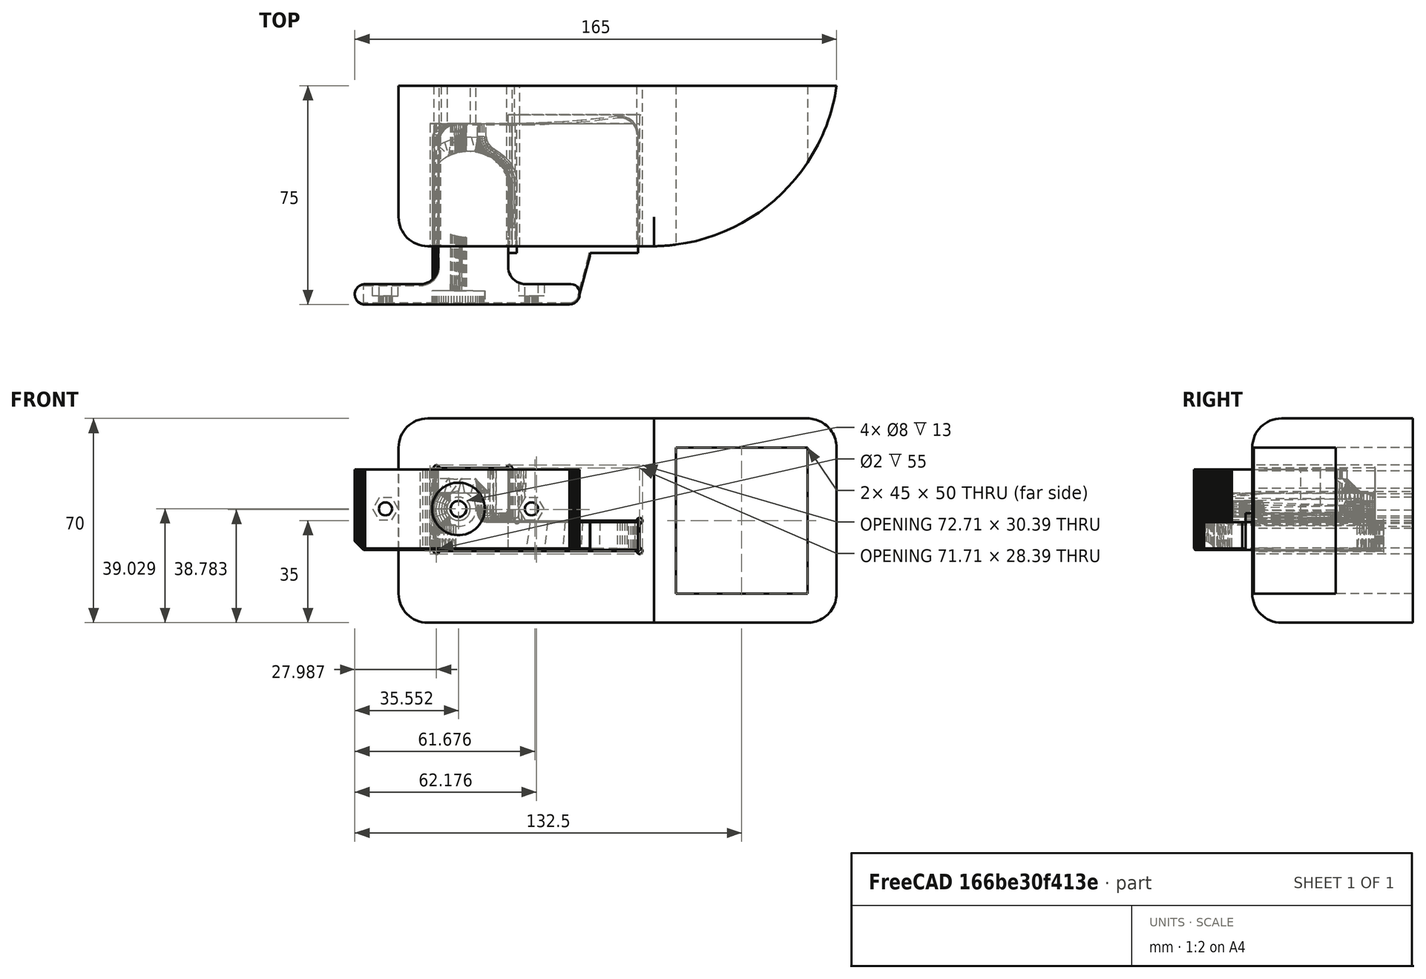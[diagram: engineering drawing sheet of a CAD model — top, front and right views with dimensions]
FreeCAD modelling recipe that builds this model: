
FCSTD DOCUMENT  (FreeCAD 0.17R7458 (Git))
Label: flexystruder_body_holderV0.7
License: CreativeCommons Attribution-ShareAlike
LicenseURL: http://creativecommons.org/licenses/by-sa/4.0/
objects: Sketcher::SketchObject×16, PartDesign::Pocket×9, PartDesign::Body×9, Part::Feature×8, PartDesign::Fillet×7, PartDesign::Pad×6, Mesh::Feature×1, PartDesign::Chamfer×1, Part::Cut×1, App::Part×1
note: 72 computed .brp shape members not serialized (recipe doc carries the construction recipe); baked Part::Feature solids carry a one-line shape summary decoded from their .brp

FEATURE [Mesh::Feature] flexystruder_body_hex_v2_0  label="flexystruder_body_hex_v2.0"
FEATURE [Part::Feature] flexystruder_body_hex_v2_0001
  shape: bbox 97.06 x 64.55 x 27.5 mm, 7934 faces, 0 solids (baked)
FEATURE [Part::Feature] flexystruder_body_hex_v2_0001001  label="flexystruder_body_hex_v2_0002"
  shape: bbox 97.06 x 64.55 x 27.5 mm, 4378 faces, 0 solids (baked)
FEATURE [Part::Feature] flexystruder_body_hex_v2_0001001_solid  label="flexystruder_body_hex_v2_0002 (Solid)"
  shape: bbox 97.06 x 64.55 x 27.5 mm, 4378 faces (baked)
FEATURE [Sketcher::SketchObject] Sketch
  MapMode = 5
  Placement = pos=(0,0,0) rot=(1,0,0;3.14159rad)
  Support = -> [flexystruder_body_hex_v2_0001001_solid]
  sketch-geometry (17):
    g0: ArcOfCircle CenterX=28 CenterY=-45.596 CenterZ=0 NormalX=0 NormalY=0 NormalZ=1 Radius=4.20615 StartAngle=4.71239 EndAngle=7.85398
    g1: ArcOfCircle CenterX=25 CenterY=-45.596 CenterZ=0 NormalX=0 NormalY=0 NormalZ=1 Radius=4.20615 StartAngle=1.5708 EndAngle=4.71239
    g2: LineSegment StartX=28 StartY=-41.3899 StartZ=0 EndX=25 EndY=-41.3899 EndZ=0
    g3: LineSegment StartX=28 StartY=-49.8022 StartZ=0 EndX=25 EndY=-49.8022 EndZ=0
    g4: ArcOfCircle CenterX=52.7327 CenterY=-58.2604 CenterZ=0 NormalX=0 NormalY=0 NormalZ=1 Radius=4.37439 StartAngle=1.5708 EndAngle=4.71239
    g5: ArcOfCircle CenterX=55.547 CenterY=-58.2604 CenterZ=0 NormalX=0 NormalY=0 NormalZ=1 Radius=4.37439 StartAngle=4.71239 EndAngle=7.85398
    g6: LineSegment StartX=52.7327 StartY=-62.6347 StartZ=0 EndX=55.547 EndY=-62.6347 EndZ=0
    g7: LineSegment StartX=52.7327 StartY=-53.886 StartZ=0 EndX=55.547 EndY=-53.886 EndZ=0
    g8: ArcOfCircle CenterX=41 CenterY=-17.6915 CenterZ=0 NormalX=0 NormalY=0 NormalZ=1 Radius=4.05397 StartAngle=4.71239 EndAngle=7.85398
    g9: ArcOfCircle CenterX=37.752 CenterY=-17.6915 CenterZ=0 NormalX=0 NormalY=0 NormalZ=1 Radius=4.05397 StartAngle=1.5708 EndAngle=4.71239
    g10: LineSegment StartX=41 StartY=-13.6375 StartZ=0 EndX=37.752 EndY=-13.6375 EndZ=0
    g11: LineSegment StartX=41 StartY=-21.7455 StartZ=0 EndX=37.752 EndY=-21.7455 EndZ=0
    g12: LineSegment StartX=23.6875 StartY=-6 StartZ=0 EndX=35.6731 EndY=-6 EndZ=0
    g13: LineSegment StartX=16.4026 StartY=-28 StartZ=0 EndX=28.3058 EndY=-28 EndZ=0
    g14: LineSegment StartX=28.3058 StartY=-28 StartZ=0 EndX=35.6731 EndY=-6 EndZ=0
    g15: LineSegment StartX=16.4026 StartY=-28 StartZ=0 EndX=16.4026 EndY=-12.5849 EndZ=0
    g16: ArcOfCircle CenterX=23.5917 CenterY=-13.2161 CenterZ=0 NormalX=0 NormalY=0 NormalZ=1 Radius=7.21677 StartAngle=1.55753 EndAngle=3.05401
  constraints (26):
    c: Tangent(g0,g3) = 1.5708
    c: Tangent(g0,g2) = -1.5708
    c: Tangent(g2,g1) = -1.5708
    c: Tangent(g3,g1) = 1.5708
    c: Horizontal(g2)
    c: Equal(g0,g1)
    c: Tangent(g4,g7) = 1.5708
    c: Tangent(g4,g6) = -1.5708
    c: Tangent(g6,g5) = -1.5708
    c: Tangent(g7,g5) = 1.5708
    c: Horizontal(g6)
    c: Equal(g4,g5)
    c: Tangent(g8,g11) = 1.5708
    c: Tangent(g8,g10) = -1.5708
    c: Tangent(g10,g9) = -1.5708
    c: Tangent(g11,g9) = 1.5708
    c: Horizontal(g10)
    c: Equal(g8,g9)
    c: Horizontal(g12)
    c: Horizontal(g13)
    c: Coincident(g14,g13)
    c: Coincident(g14,g12)
    c: Coincident(g15,g13)
    c: Vertical(g15)
    c: Coincident(g16,g12)
    c: Coincident(g16,g15)
FEATURE [PartDesign::Pad] Pad
  BaseFeature = -> flexystruder_body_hex_v2_0001001_solid
  Length = 9.5
  Length2 = 100
  Profile = -> Sketch
  Reversed = true
  Type = 0
FEATURE [Sketcher::SketchObject] Sketch001
  ExternalGeometry = -> [Pad]
  MapMode = 5
  Placement = pos=(17.5,0,0) rot=(0.57735,0.57735,0.57735;2.0944rad)
  Support = -> [Pad]
  sketch-geometry (4):
    g0: LineSegment StartX=26.5 StartY=12.5 StartZ=0 EndX=17.6702 EndY=12.5 EndZ=0
    g1: LineSegment StartX=17.6702 StartY=12.5 StartZ=0 EndX=17.6702 EndY=9.5 EndZ=0
    g2: LineSegment StartX=17.6702 StartY=9.5 StartZ=0 EndX=26.5 EndY=9.5 EndZ=0
    g3: LineSegment StartX=26.5 StartY=9.5 StartZ=0 EndX=26.5 EndY=12.5 EndZ=0
  constraints (10):
    c: Coincident(g0,g1)
    c: Coincident(g1,g2)
    c: Coincident(g2,g3)
    c: Coincident(g3,g0)
    c: Horizontal(g0)
    c: Horizontal(g2)
    c: Vertical(g1)
    c: Vertical(g3)
    c: Coincident(g0,g-4)
    c: PointOnObject(g1,g-3)
FEATURE [PartDesign::Pad] Pad001
  BaseFeature = -> Pad
  Length = 3
  Length2 = 100
  Profile = -> Sketch001
  Type = 0
FEATURE [PartDesign::Chamfer] Chamfer
  Base = -> Pad001 [Edge1475]
  BaseFeature = -> Pad001
  Size = 2.9
FEATURE [Sketcher::SketchObject] Sketch002
  ExternalGeometry = -> [Chamfer]
  MapMode = 5
  Placement = pos=(0,0,27.5) rot=(0,0,1;0rad)
  Support = -> [Chamfer]
  sketch-geometry (4):
    g0: LineSegment StartX=-6.5 StartY=48.2121 StartZ=0 EndX=-6.5 EndY=27.0119 EndZ=0
    g1: ArcOfCircle CenterX=3.84323 CenterY=38.0759 CenterZ=0 NormalX=0 NormalY=0 NormalZ=1 Radius=14.4819 StartAngle=0.364009 EndAngle=2.3663
    g2: LineSegment StartX=17.3762 StartY=43.2318 StartZ=0 EndX=17.5 EndY=37.4236 EndZ=0
    g3: ArcOfCircle CenterX=3.40646 CenterY=37.0436 CenterZ=0 NormalX=0 NormalY=0 NormalZ=1 Radius=14.0987 StartAngle=3.93327 EndAngle=6.31015
  constraints (10):
    c: Vertical(g0)
    c: Coincident(g0,g-5)
    c: Coincident(g0,g-6)
    c: Coincident(g1,g0)
    c: Coincident(g1,g-9)
    c: PointOnObject(g-21,g1)
    c: Coincident(g2,g1)
    c: Coincident(g2,g-7)
    c: Coincident(g3,g0)
    c: Coincident(g3,g2)
FEATURE [PartDesign::Pad] Pad002
  BaseFeature = -> Chamfer
  Length = 10
  Length2 = 100
  Profile = -> Sketch002
  Reversed = true
  Type = 3
  UpToFace = -> Chamfer [Face709]
FEATURE [Sketcher::SketchObject] Sketch003
  ExternalGeometry = -> [Pad002]
  MapMode = 5
  Placement = pos=(0,0,0) rot=(1,0,0;3.14159rad)
  Support = -> [Pad002]
  sketch-geometry (4):
    g0: LineSegment StartX=62.0584 StartY=-58.2729 StartZ=0 EndX=17.5 EndY=-58.2729 EndZ=0
    g1: LineSegment StartX=17.5 StartY=-58.2729 StartZ=0 EndX=17.5 EndY=-17.6702 EndZ=0
    g2: LineSegment StartX=17.5 StartY=-17.6702 StartZ=0 EndX=62.0584 EndY=-17.6702 EndZ=0
    g3: LineSegment StartX=62.0584 StartY=-17.6702 StartZ=0 EndX=62.0584 EndY=-58.2729 EndZ=0
  constraints (10):
    c: Coincident(g0,g1)
    c: Coincident(g1,g2)
    c: Coincident(g2,g3)
    c: Coincident(g3,g0)
    c: Horizontal(g0)
    c: Horizontal(g2)
    c: Vertical(g1)
    c: Vertical(g3)
    c: Coincident(g0,g-3)
    c: Coincident(g1,g-4)
FEATURE [PartDesign::Pad] Pad003
  BaseFeature = -> Pad002
  Length = 9.5
  Length2 = 100
  Profile = -> Sketch003
  Reversed = true
  Type = 0
FEATURE [Sketcher::SketchObject] Sketch005
  MapMode = 5
  Placement = pos=(0,0,0) rot=(0.57735,0.57735,0.57735;2.0944rad)
  Support = -> [YZ_Plane003]
  sketch-geometry (4):
    g0: LineSegment StartX=20 StartY=45 StartZ=0 EndX=75 EndY=45 EndZ=0
    g1: LineSegment StartX=75 StartY=45 StartZ=0 EndX=75 EndY=-25 EndZ=0
    g2: LineSegment StartX=75 StartY=-25 StartZ=0 EndX=20 EndY=-25 EndZ=0
    g3: LineSegment StartX=20 StartY=-25 StartZ=0 EndX=20 EndY=45 EndZ=0
  constraints (12):
    c: Coincident(g0,g1)
    c: Coincident(g1,g2)
    c: Coincident(g2,g3)
    c: Coincident(g3,g0)
    c: Horizontal(g0)
    c: Horizontal(g2)
    c: Vertical(g1)
    c: Vertical(g3)
    c: DistanceY(g1) = -70
    c: DistanceY(g-1,g2) = -25
    c: DistanceX(g-1,g1) = 75
    c: DistanceX(g2) = -55
FEATURE [PartDesign::Pad] Pad004002
  Length = 130
  Length2 = 20
  Placement = pos=(0,0,0) rot=(0.57735,0.57735,0.57735;2.0944rad)
  Profile = -> Sketch005
  Type = 4
FEATURE [Sketcher::SketchObject] Sketch011
  MapMode = 5
  Placement = pos=(0,62,0) rot=(1,0,0;1.5708rad)
  sketch-geometry (1):
    g0: Circle CenterX=0.546326 CenterY=14.034 CenterZ=0 NormalX=0 NormalY=0 NormalZ=1 Radius=4.18499
FEATURE [Part::Feature] Pocket003001  label="Pocket004"
  shape: bbox 155.2 x 62.65 x 70 mm, 98 faces (baked)
FEATURE [Sketcher::SketchObject] Sketch004
  ExternalGeometry = -> [Pad003]
  MapMode = 5
  Placement = pos=(0,20,0) rot=(1,0,0;1.5708rad)
  Support = -> [Pocket003001]
  constraints (10):
    c: Coincident(g0,g1)
    c: Coincident(g1,g2)
    c: Coincident(g2,g3)
    c: Coincident(g3,g0)
    c: Horizontal(g0)
    c: Horizontal(g2)
    c: Vertical(g1)
    c: Vertical(g3)
    c: Coincident(g0,g-4)
    c: Coincident(g1,g-3)
FEATURE [PartDesign::Pad] Pad004
  BaseFeature = -> Pocket003001
  Length = 1
  Length2 = 100
  Profile = -> Sketch004
  Reversed = true
  Type = 0
FEATURE [Sketcher::SketchObject] Sketch012
  MapMode = 5
  Placement = pos=(0,20,0) rot=(1,0,0;1.5708rad)
  Support = -> [Pocket003001]
  sketch-geometry (3):
    g0: LineSegment StartX=17.5433 StartY=12.8629 StartZ=0 EndX=21.0794 EndY=9.39905 EndZ=0
    g1: LineSegment StartX=21.0794 StartY=9.39905 StartZ=0 EndX=17.4196 EndY=9.04442 EndZ=0
    g2: LineSegment StartX=17.4196 StartY=9.04442 StartZ=0 EndX=17.5433 EndY=12.8629 EndZ=0
  constraints (3):
    c: Coincident(g0,g1)
    c: Coincident(g1,g2)
    c: Coincident(g2,g0)
FEATURE [PartDesign::Pocket] Pocket003002
  BaseFeature = -> Pocket003001
  Length = 5
  Profile = -> Sketch012
  Type = 2
FEATURE [Part::Feature] Pocket003002001  label="Pocket003003"
  shape: bbox 155.2 x 62.65 x 70 mm, 96 faces (baked)
FEATURE [Sketcher::SketchObject] Sketch013
  ExternalGeometry = -> [Pocket003002001]
  MapMode = 5
  Placement = pos=(0,62,0) rot=(1,0,0;1.5708rad)
  Support = -> [Pocket003002001]
  sketch-geometry (4):
    g0: LineSegment StartX=62.5298 StartY=-0.412097 StartZ=0 EndX=17.5 EndY=-0.412097 EndZ=0
    g1: LineSegment StartX=17.5 StartY=-0.412097 StartZ=0 EndX=17.5 EndY=9.93195 EndZ=0
    g2: LineSegment StartX=17.5 StartY=9.93195 StartZ=0 EndX=62.5298 EndY=9.93195 EndZ=0
    g3: LineSegment StartX=62.5298 StartY=9.93195 StartZ=0 EndX=62.5298 EndY=-0.412097 EndZ=0
  constraints (11):
    c: Coincident(g0,g1)
    c: Coincident(g1,g2)
    c: Coincident(g2,g3)
    c: Coincident(g3,g0)
    c: Horizontal(g0)
    c: Horizontal(g2)
    c: Vertical(g1)
    c: Vertical(g3)
    c: Coincident(g0,g-5)
    c: PointOnObject(g-3,g2)
    c: PointOnObject(g-4,g1)
FEATURE [PartDesign::Pocket] Pocket003002002
  BaseFeature = -> Pocket003002001
  Length = 3
  Profile = -> Sketch013
  Type = 0
FEATURE [Sketcher::SketchObject] Sketch014
  ExternalGeometry = -> [Pocket003002002]
  MapMode = 5
  Placement = pos=(0,20,0) rot=(1,0,0;1.5708rad)
  Support = -> [Pocket003002002]
  sketch-geometry (9):
    g0: Circle CenterX=17.9124 CenterY=12.5014 CenterZ=0 NormalX=0 NormalY=0 NormalZ=1 Radius=1
    g1: Circle CenterX=20.5354 CenterY=9.93195 CenterZ=0 NormalX=0 NormalY=0 NormalZ=1 Radius=1
    g2: Circle CenterX=62.5298 CenterY=9.93195 CenterZ=0 NormalX=0 NormalY=0 NormalZ=1 Radius=1
    g3: Circle CenterX=62.5298 CenterY=-0.412097 CenterZ=0 NormalX=0 NormalY=0 NormalZ=1 Radius=1
    g4: Circle CenterX=-7.01255 CenterY=-0.412097 CenterZ=0 NormalX=0 NormalY=0 NormalZ=1 Radius=1
    g5: Circle CenterX=-7.01255 CenterY=8.30665 CenterZ=0 NormalX=0 NormalY=0 NormalZ=1 Radius=1
    g6: Circle CenterX=-7.01858 CenterY=20.0686 CenterZ=0 NormalX=0 NormalY=0 NormalZ=1 Radius=1
    g7: Circle CenterX=-7.01858 CenterY=27.9783 CenterZ=0 NormalX=0 NormalY=0 NormalZ=1 Radius=1
    g8: Circle CenterX=17.9124 CenterY=27.9783 CenterZ=0 NormalX=0 NormalY=0 NormalZ=1 Radius=1
  constraints (18):
    c: Coincident(g0,g-4)
    c: Coincident(g1,g-5)
    c: Coincident(g2,g-6)
    c: Coincident(g3,g-7)
    c: Coincident(g4,g-7)
    c: Coincident(g5,g-8)
    c: Coincident(g6,g-8)
    c: Coincident(g7,g-3)
    c: Coincident(g8,g-4)
    c: Radius(g7) = 1
    c: Equal(g7,g6)
    c: Equal(g7,g5)
    c: Equal(g7,g4)
    c: Equal(g7,g1)
    c: Equal(g7,g0)
    c: Equal(g7,g8)
    c: Equal(g7,g2)
    c: Equal(g7,g3)
FEATURE [PartDesign::Pocket] Pocket003002003
  BaseFeature = -> Pocket003002002
  Length = 0
  Profile = -> Sketch014
  Type = 1
FEATURE [Part::Feature] Pocket003002003001  label="Pocket003002004"
  shape: bbox 155.2 x 62.65 x 70 mm, 57 faces (baked)
FEATURE [PartDesign::Fillet] Fillet001
  Base = -> Pocket003002003001 [Edge94,Edge89,Edge98,Edge96]
  BaseFeature = -> Pocket003002003001
  Radius = 1
FEATURE [Part::Feature] Fillet001001  label="Fillet002"
  shape: bbox 155.2 x 62.65 x 70 mm, 61 faces (baked)
FEATURE [PartDesign::Fillet] Fillet001002
  Base = -> Fillet001001 [Edge115,Edge114]
  BaseFeature = -> Fillet001001
  Radius = 1
FEATURE [PartDesign::Fillet] Fillet001003
  Base = -> Fillet001002 [Edge56,Edge60]
  BaseFeature = -> Fillet001002
  Radius = 1
FEATURE [PartDesign::Fillet] Fillet001004
  Base = -> Fillet001003 [Edge92,Edge96,Edge110,Edge114]
  BaseFeature = -> Fillet001003
  Radius = 1
FEATURE [PartDesign::Fillet] Fillet001005
  Base = -> Fillet001004 [Edge56,Edge59]
  BaseFeature = -> Fillet001004
  Radius = 1
FEATURE [PartDesign::Fillet] Fillet001006
  Base = -> Fillet001005 [Edge65,Edge74]
  BaseFeature = -> Fillet001005
  Radius = 1
FEATURE [Sketcher::SketchObject] Sketch015
  ExternalGeometry = -> [Fillet001006]
  MapMode = 5
  Placement = pos=(0,20,0) rot=(1,0,0;1.5708rad)
  Support = -> [Fillet001006]
  sketch-geometry (4):
    g0: ArcOfCircle CenterX=-5.59815 CenterY=-0.909281 CenterZ=0 NormalX=0 NormalY=0 NormalZ=1 Radius=0.5 StartAngle=1.46461 EndAngle=2.84847
    g1: ArcOfCircle CenterX=-7.51255 CenterY=1.00212 CenterZ=0 NormalX=0 NormalY=0 NormalZ=1 Radius=0.5 StartAngle=5.05223 EndAngle=6.28319
    g2: ArcOfCircle CenterX=-6.21326 CenterY=0.370879 CenterZ=0 NormalX=0 NormalY=0 NormalZ=1 Radius=1.14385 StartAngle=3.0014 EndAngle=4.83195
    g3: LineSegment StartX=-7.01255 StartY=1.00212 StartZ=0 EndX=-5.54516 EndY=-0.412097 EndZ=0
  constraints (10):
    c: PointOnObject(g0,g-3)
    c: PointOnObject(g0,g-5)
    c: Radius(g0) = 0.5
    c: PointOnObject(g1,g-3)
    c: PointOnObject(g1,g-4)
    c: Radius(g1) = 0.5
    c: Coincident(g2,g0)
    c: Coincident(g3,g1)
    c: Coincident(g3,g0)
    c: Coincident(g1,g2)
FEATURE [PartDesign::Pocket] Pocket003002003002
  BaseFeature = -> Fillet001006
  Length = 42
  Profile = -> Sketch015
  Type = 0
FEATURE [Part::Feature] Pocket003002003002001  label="Pocket003002003003"
  shape: bbox 155.2 x 62.65 x 70 mm, 75 faces (baked)
FEATURE [PartDesign::Body] Pad003Body
  BaseFeature = -> flexystruder_body_hex_v2_0001001_solid
  Model = -> [Sketch,Pad,Sketch001,Pad001,Chamfer,Sketch002,Pad002,Sketch003,Pad003]
  Origin = -> Pad003BodyOrigin
  Tip = -> Pad003
FEATURE [PartDesign::Body] Pad004Body
  BaseFeature = -> Pocket003001
  Model = -> [Sketch004,Pad004]
  Origin = -> Pad004BodyOrigin
  Tip = -> Pad004
FEATURE [PartDesign::Body] Pad004002Body
  Model = -> [Sketch005,Pad004002]
  Origin = -> Pad004002BodyOrigin
  Tip = -> Pad004002
FEATURE [Part::Cut] Cut
  Base = -> Pad004002Body
FEATURE [Sketcher::SketchObject] Sketch006
  ExternalGeometry = -> [Cut]
  MapMode = 5
  Placement = pos=(0,0,45) rot=(0,0,1;0rad)
  Support = -> [Cut]
  sketch-geometry (3):
    g0: ArcOfCircle CenterX=66.7062 CenterY=83.914 CenterZ=0 NormalX=0 NormalY=0 NormalZ=1 Radius=63.9184 StartAngle=4.72413 EndAngle=6.14327
    g1: LineSegment StartX=130 StartY=75 StartZ=0 EndX=130 EndY=20 EndZ=0
    g2: LineSegment StartX=130 StartY=20 StartZ=0 EndX=67.4569 EndY=20 EndZ=0
  constraints (8):
    c: Coincident(g1,g0)
    c: Coincident(g1,g-4)
    c: Vertical(g1)
    c: Coincident(g2,g1)
    c: Coincident(g2,g0)
    c: Horizontal(g2)
    c: Coincident(g0,g-3)
    c: Coincident(g1,g-3)
FEATURE [PartDesign::Pocket] Pocket
  BaseFeature = -> Cut
  Length = 5
  Profile = -> Sketch006
  Type = 1
FEATURE [PartDesign::Fillet] Fillet
  Base = -> Pocket [Edge3,Edge4,Edge1,Edge7,Edge6,Edge10,Edge12]
  BaseFeature = -> Pocket
  Radius = 10
FEATURE [Sketcher::SketchObject] Sketch007
  MapMode = 5
  Placement = pos=(0,20,0) rot=(1,0,0;1.5708rad)
  Support = -> [Fillet]
  sketch-geometry (1):
    g0: Circle CenterX=0.551868 CenterY=14.0293 CenterZ=0 NormalX=0 NormalY=0 NormalZ=1 Radius=4
  constraints (1):
    c: Radius(g0) = 4
FEATURE [PartDesign::Pocket] Pocket001
  BaseFeature = -> Fillet
  Length = 5
  Profile = -> Sketch007
  Type = 1
FEATURE [Sketcher::SketchObject] Sketch008
  MapMode = 5
  Placement = pos=(0,75,0) rot=(0,0.707107,0.707107;3.14159rad)
  Support = -> [Pocket001]
  sketch-geometry (4):
    g0: LineSegment StartX=-120 StartY=35 StartZ=0 EndX=-75 EndY=35 EndZ=0
    g1: LineSegment StartX=-75 StartY=35 StartZ=0 EndX=-75 EndY=-15 EndZ=0
    g2: LineSegment StartX=-75 StartY=-15 StartZ=0 EndX=-120 EndY=-15 EndZ=0
    g3: LineSegment StartX=-120 StartY=-15 StartZ=0 EndX=-120 EndY=35 EndZ=0
  constraints (8):
    c: Coincident(g0,g1)
    c: Coincident(g1,g2)
    c: Coincident(g2,g3)
    c: Coincident(g3,g0)
    c: Horizontal(g0)
    c: Horizontal(g2)
    c: Vertical(g1)
    c: Vertical(g3)
FEATURE [PartDesign::Pocket] Pocket002
  BaseFeature = -> Pocket001
  Length = 5
  Profile = -> Sketch008
  Type = 1
FEATURE [Sketcher::SketchObject] Sketch009
  MapMode = 5
  Placement = pos=(0,20,0) rot=(1,0,0;1.5708rad)
  Support = -> [Pocket002]
  sketch-geometry (9):
    g0: LineSegment StartX=20.4681 StartY=9.93195 StartZ=0 EndX=62.5298 EndY=9.93195 EndZ=0
    g1: LineSegment StartX=62.5298 StartY=9.93195 StartZ=0 EndX=62.5298 EndY=-0.412097 EndZ=0
    g2: LineSegment StartX=-7.01255 StartY=-0.412097 StartZ=0 EndX=-7.01255 EndY=8.30665 EndZ=0
    g3: LineSegment StartX=-7.01858 StartY=20.0686 StartZ=0 EndX=-7.01858 EndY=27.9783 EndZ=0
    g4: LineSegment StartX=-7.01858 StartY=27.9783 StartZ=0 EndX=17.9124 EndY=27.9783 EndZ=0
    g5: LineSegment StartX=17.9124 StartY=27.9783 StartZ=0 EndX=17.9124 EndY=12.3928 EndZ=0
    g6: ArcOfCircle CenterX=20.8446 CenterY=12.8805 CenterZ=0 NormalX=0 NormalY=0 NormalZ=1 Radius=2.97245 StartAngle=3.30639 EndAngle=4.5854
    g7: ArcOfCircle CenterX=-0.0992204 CenterY=14.1912 CenterZ=0 NormalX=0 NormalY=0 NormalZ=1 Radius=9.07863 StartAngle=2.43744 EndAngle=3.84677
    g8: LineSegment StartX=-7.01255 StartY=-0.412097 StartZ=0 EndX=62.5298 EndY=-0.412097 EndZ=0
  constraints (16):
    c: Coincident(g0,g1)
    c: Coincident(g3,g4)
    c: Coincident(g4,g5)
    c: Vertical(g2)
    c: Vertical(g3)
    c: Vertical(g5)
    c: Vertical(g1)
    c: Horizontal(g0)
    c: Coincident(g6,g5)
    c: Coincident(g6,g0)
    c: Horizontal(g4)
    c: Coincident(g7,g3)
    c: Coincident(g7,g2)
    c: Coincident(g8,g2)
    c: Coincident(g8,g1)
    c: Horizontal(g8)
FEATURE [PartDesign::Pocket] Pocket003
  BaseFeature = -> Pocket002
  Length = 42
  Profile = -> Sketch009
  Type = 0
FEATURE [PartDesign::Body] Pocket003Body
  BaseFeature = -> Cut
  Model = -> [Sketch006,Pocket,Fillet,Sketch007,Pocket001,Sketch008,Pocket002,Sketch009,Pocket003]
  Origin = -> Pocket003BodyOrigin
  Tip = -> Pocket003
FEATURE [PartDesign::Body] Pocket003002Body
  BaseFeature = -> Pocket003001
  Model = -> [Sketch012,Pocket003002]
  Origin = -> Pocket003002BodyOrigin
  Tip = -> Pocket003002
FEATURE [PartDesign::Body] Pocket003002003Body
  BaseFeature = -> Pocket003002001
  Model = -> [Sketch013,Pocket003002002,Sketch014,Pocket003002003]
  Origin = -> Pocket003002003BodyOrigin
  Tip = -> Pocket003002003
FEATURE [PartDesign::Body] Fillet001Body
  BaseFeature = -> Pocket003002003001
  Model = -> [Fillet001]
  Origin = -> Fillet001BodyOrigin
  Tip = -> Fillet001
FEATURE [PartDesign::Body] Pocket003002003002Body
  BaseFeature = -> Fillet001001
  Model = -> [Fillet001002,Fillet001003,Fillet001004,Fillet001005,Fillet001006,Sketch015,Pocket003002003002]
  Origin = -> Pocket003002003002BodyOrigin
  Tip = -> Pocket003002003002
FEATURE [Sketcher::SketchObject] Sketch016
  ExternalGeometry = -> [Pocket003002003002001]
  MapMode = 5
  Placement = pos=(0,75,0) rot=(0,0.707107,0.707107;3.14159rad)
  Support = -> [Pocket003002003002001]
  sketch-geometry (1):
    g0: Circle CenterX=-0.551868 CenterY=14.0293 CenterZ=0 NormalX=0 NormalY=0 NormalZ=1 Radius=6
  constraints (2):
    c: Coincident(g0,g-3)
    c: Radius(g0) = 6
FEATURE [PartDesign::Pocket] Pocket003002003002002
  BaseFeature = -> Pocket003002003002001
  Length = 5
  Profile = -> Sketch016
  Type = 1
FEATURE [PartDesign::Body] Body
  BaseFeature = -> Pocket003002003002001
  Model = -> [Sketch016,Pocket003002003002002]
  Origin = -> BodyOrigin
  Tip = -> Pocket003002003002002
FEATURE [App::Part] Part
  Group = -> [Pad003Body,Pad004Body,Pad004002Body,Pocket003Body,Pocket003002Body,Pocket003002003Body,Fillet001Body,Pocket003002003002Body,Body]
  License = CC BY 3.0
  LicenseURL = http://creativecommons.org/licenses/by/3.0/
  Origin = -> PartOrigin
